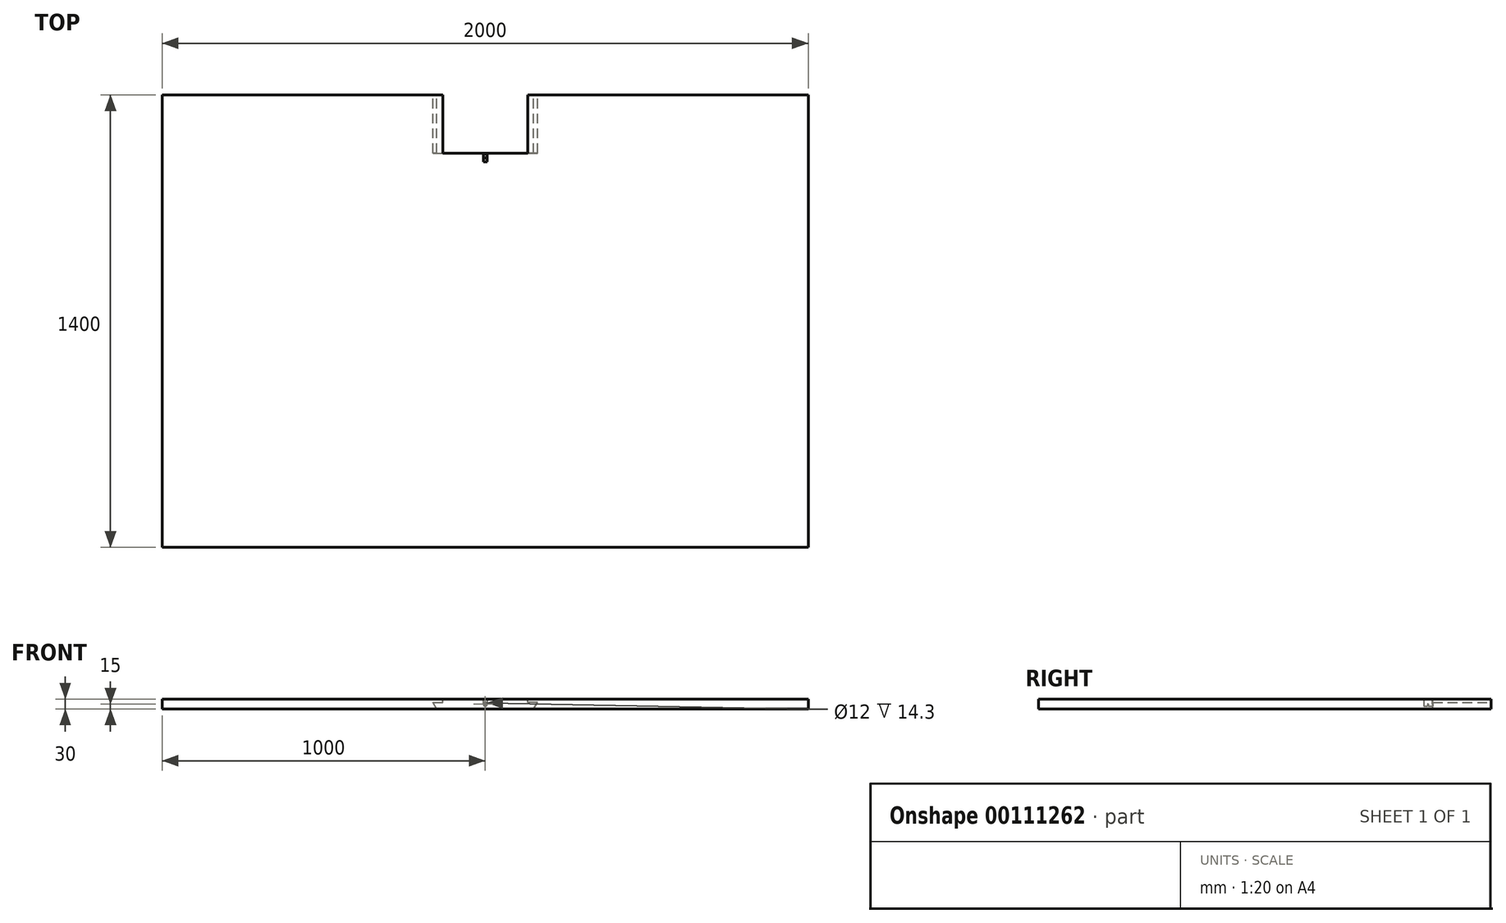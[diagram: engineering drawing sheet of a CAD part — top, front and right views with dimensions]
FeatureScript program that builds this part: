
annotation { "Feature Type Name" : "Feature", "Feature Type Description" : "" }
export const myFeature = defineFeature(function(context is Context, id is Id, definition is map)
    precondition{}
    {
        {
            var Q0;
            Q0=qCreatedBy(makeId("Top.planeOp"),FACE);
            var sketch = newSketch(context, id + "F0", { "sketchPlane" : qUnion([Q0]), "disableImprinting" : false});
            skLineSegment(sketch, "E0.bottom", {"start": v(-1000, 700) * mm, "end": v(1000, 700) * mm});
            skLineSegment(sketch, "E0.top", {"start": v(-1000, -700) * mm, "end": v(1000, -700) * mm});
            skLineSegment(sketch, "E0.left", {"start": v(-1000, 700) * mm, "end": v(-1000, -700) * mm});
            skLineSegment(sketch, "E0.right", {"start": v(1000, 700) * mm, "end": v(1000, -700) * mm});
            skPoint(sketch, "E0.middle", {"position": v(0, 0) * mm});
            skSolve(sketch);
        }
        {
            var Q0;
            Q0=makeQuery(id+"F0.imprint","IMPRINT",FACE,{"disambiguationData":[TD([[makeQuery(id+"F0.imprint","IMPRINT",EDGE,{"derivedFrom":sQuery(id+"F0.wireOp",EDGE,"E0.bottom")}),-1.0]])]});
            extrude(context, id + "F1", {"entities" : qUnion([Q0]), "depth" : 30 * mm});
        }
        {
            var Q0;
            Q0=makeQuery(id+"F1.opExtrude","SWEPT_FACE",FACE,{"disambiguationData":[OSD([sQuery(id+"F0.wireOp",EDGE,"E0.bottom")])]});
            var sketch = newSketch(context, id + "F2", { "sketchPlane" : qUnion([Q0])});
            skLineSegment(sketch, "E1", {"start": v(-150, 0) * mm, "end": v(-161.55, 20) * mm});
            skLineSegment(sketch, "E2", {"start": v(-161.55, 20) * mm, "end": v(-131.55, 20) * mm});
            skLineSegment(sketch, "E3", {"start": v(-131.55, 20) * mm, "end": v(-131.55, 30) * mm});
            skLineSegment(sketch, "E4", {"start": v(0, 0) * mm, "end": v(0, 30) * mm, "construction": true});
            skLineSegment(sketch, "E5.MirrorCS", {"start": v(131.55, 20) * mm, "end": v(131.55, 30) * mm});
            skLineSegment(sketch, "E6.MirrorCS", {"start": v(161.55, 20) * mm, "end": v(131.55, 20) * mm});
            skLineSegment(sketch, "E7.MirrorCS", {"start": v(150, 0) * mm, "end": v(161.55, 20) * mm});
            skLineSegment(sketch, "E8", {"start": v(131.55, 30) * mm, "end": v(-131.55, 30) * mm});
            skLineSegment(sketch, "E9", {"start": v(150, 0) * mm, "end": v(-150, 0) * mm});
            skSolve(sketch);
        }
        {
            var Q0;
            Q0=qSketchRegion(id+"F2",true);
            extrude(context, id + "F3", {"entities" : qUnion([Q0]), "operationType" : NewBodyOperationType.REMOVE, "oppositeDirection" : true, "depth" : 180 * mm});
        }
        {
            var Q0;
            Q0=makeQuery(id+"F3.boolean.opBoolean","COPY",FACE,{"derivedFrom":makeQuery(id+"F3.opExtrude","CAP_FACE",FACE,{"disambiguationData":[OSD([sQuery(id+"F2.wireOp",EDGE,"E1"),sQuery(id+"F2.wireOp",EDGE,"E2"),sQuery(id+"F2.wireOp",EDGE,"E3"),sQuery(id+"F2.wireOp",EDGE,"E5.MirrorCS"),sQuery(id+"F2.wireOp",EDGE,"E6.MirrorCS"),sQuery(id+"F2.wireOp",EDGE,"E7.MirrorCS"),sQuery(id+"F2.wireOp",EDGE,"E8"),sQuery(id+"F2.wireOp",EDGE,"E9")])],"isStart":false})});
            var sketch = newSketch(context, id + "F4", { "sketchPlane" : qUnion([Q0])});
            skLineSegment(sketch, "E10", {"start": v(0, 0) * mm, "end": v(0, 30) * mm, "construction": true});
            skCircle(sketch, "E11", {"center": v(0, 15) * mm, "radius": 6 * mm});
            skSolve(sketch);
        }
        {
            var Q0;
            Q0 = qSketchRegion(id + "F4", true);
            extrude(context, id + "F5", {"entities" : qUnion([Q0]), "operationType" : NewBodyOperationType.REMOVE, "oppositeDirection" : true, "depth" : 20 * mm});
        }
        {
            var Q0;
            Q0=makeQuery(id+"F1.opExtrude","CAP_FACE",FACE,{"disambiguationData":[OSD([sQuery(id+"F0.wireOp",EDGE,"E0.bottom"),sQuery(id+"F0.wireOp",EDGE,"E0.top"),sQuery(id+"F0.wireOp",EDGE,"E0.left"),sQuery(id+"F0.wireOp",EDGE,"E0.right")])],"isStart":true});
            var sketch = newSketch(context, id + "F6", { "sketchPlane" : qUnion([Q0])});
            skLineSegment(sketch, "E12.0", {"start": v(-150, -520) * mm, "end": v(150, -520) * mm, "construction": true});
            skLineSegment(sketch, "E13", {"start": v(0, -520) * mm, "end": v(0, -505) * mm, "construction": true});
            skPoint(sketch, "E13.endSnap0", {"position": v(0, -520) * mm});
            skLineSegment(sketch, "E14.bottom", {"start": v(20, -500) * mm, "end": v(-20, -500) * mm});
            skLineSegment(sketch, "E14.top", {"start": v(20, -510) * mm, "end": v(-20, -510) * mm});
            skLineSegment(sketch, "E14.left", {"start": v(20, -500) * mm, "end": v(20, -510) * mm});
            skLineSegment(sketch, "E14.right", {"start": v(-20, -500) * mm, "end": v(-20, -510) * mm});
            skPoint(sketch, "E14.middle", {"position": v(0, -505) * mm});
            skSolve(sketch);
        }
        {
            var Q0;
            Q0=makeQuery(id+"F6.imprint","IMPRINT",FACE,{"disambiguationData":[TD([[makeQuery(id+"F6.imprint","IMPRINT",EDGE,{"derivedFrom":sQuery(id+"F6.wireOp",EDGE,"E14.bottom")}),1.0]])]});
            extrude(context, id + "F7", {"entities" : qUnion([Q0]), "operationType" : NewBodyOperationType.REMOVE, "oppositeDirection" : true, "depth" : 2 * mm});
        }
        {
            var Q0;
            Q0=makeQuery(id+"F3.boolean.opBoolean","COPY",FACE,{"derivedFrom":makeQuery(id+"F3.opExtrude","CAP_FACE",FACE,{"disambiguationData":[OSD([sQuery(id+"F2.wireOp",EDGE,"E1"),sQuery(id+"F2.wireOp",EDGE,"E2"),sQuery(id+"F2.wireOp",EDGE,"E3"),sQuery(id+"F2.wireOp",EDGE,"E5.MirrorCS"),sQuery(id+"F2.wireOp",EDGE,"E6.MirrorCS"),sQuery(id+"F2.wireOp",EDGE,"E7.MirrorCS"),sQuery(id+"F2.wireOp",EDGE,"E8"),sQuery(id+"F2.wireOp",EDGE,"E9")])],"isStart":false})});
            cPlane(context, id + "F8", {"entities" : qUnion([Q0]), "cplaneType" : CPlaneType.OFFSET, "offset" : 15 * mm, "oppositeDirection" : true, "width" : 150 * mm, "height" : 150 * mm});
        }
        {
            var Q0;
            Q0=makeQuery(id+"F7.boolean.opBoolean","COPY",FACE,{"derivedFrom":makeQuery(id+"F7.opExtrude","CAP_FACE",FACE,{"disambiguationData":[OSD([sQuery(id+"F6.wireOp",EDGE,"E14.bottom"),sQuery(id+"F6.wireOp",EDGE,"E14.top"),sQuery(id+"F6.wireOp",EDGE,"E14.left"),sQuery(id+"F6.wireOp",EDGE,"E14.right")])],"isStart":false})});
            var sketch = newSketch(context, id + "F9", { "sketchPlane" : qUnion([Q0])});
            skLineSegment(sketch, "E15.bottom", {"start": v(20, -500) * mm, "end": v(-20, -500) * mm});
            skLineSegment(sketch, "E15.top", {"start": v(20, -510) * mm, "end": v(-20, -510) * mm});
            skLineSegment(sketch, "E15.left", {"start": v(20, -500) * mm, "end": v(20, -510) * mm});
            skLineSegment(sketch, "E15.right", {"start": v(-20, -500) * mm, "end": v(-20, -510) * mm});
            skLineSegment(sketch, "E16.0", {"start": v(18.5, -501.5) * mm, "end": v(-18.5, -501.5) * mm});
            skLineSegment(sketch, "E16.1", {"start": v(18.5, -501.5) * mm, "end": v(18.5, -508.5) * mm});
            skLineSegment(sketch, "E16.2", {"start": v(18.5, -508.5) * mm, "end": v(-18.5, -508.5) * mm});
            skLineSegment(sketch, "E16.3", {"start": v(-18.5, -501.5) * mm, "end": v(-18.5, -508.5) * mm});
            skSolve(sketch);
        }
        {
            var Q0;
            Q0=makeQuery(id+"F9.imprint","IMPRINT",FACE,{"disambiguationData":[TD([[makeQuery(id+"F9.imprint","IMPRINT",EDGE,{"derivedFrom":sQuery(id+"F9.wireOp",EDGE,"E16.0")}),1.0]])]});
            extrude(context, id + "F10", {"entities" : qUnion([Q0]), "operationType" : NewBodyOperationType.REMOVE, "endBound" : BoundingType.THROUGH_ALL, "oppositeDirection" : true, "depth" : 25 * mm});
        }
        {
            var Q0;
            Q0=qCreatedBy(id+"F8.planeOp",FACE);
            var sketch = newSketch(context, id + "F11", { "sketchPlane" : qUnion([Q0])});
            skCircle(sketch, "E17.0", {"center": v(0, 15) * mm, "radius": 6 * mm});
            skCircle(sketch, "E18", {"center": v(0, 15) * mm, "radius": 4.5 * mm});
            skLineSegment(sketch, "E19", {"start": v(6, 15) * mm, "end": v(-6, 15) * mm});
            skLineSegment(sketch, "E20", {"start": v(6, 15) * mm, "end": v(6, 30) * mm});
            skLineSegment(sketch, "E21", {"start": v(6, 30) * mm, "end": v(-6, 30) * mm});
            skLineSegment(sketch, "E22", {"start": v(-6, 30) * mm, "end": v(-6, 15) * mm});
            skSolve(sketch);
        }
        {
            var Q0;
            Q0 = qSketchRegion(id + "F6", true);
            var Q1;
            Q1=makeQuery(id+"F7.boolean.opBoolean","COPY",FACE,{"derivedFrom":makeQuery(id+"F7.opExtrude","CAP_FACE",FACE,{"disambiguationData":[OSD([sQuery(id+"F6.wireOp",EDGE,"E14.bottom"),sQuery(id+"F6.wireOp",EDGE,"E14.top"),sQuery(id+"F6.wireOp",EDGE,"E14.left"),sQuery(id+"F6.wireOp",EDGE,"E14.right")])],"isStart":false})});
            extrude(context, id + "F12", {"entities" : qUnion([Q0]), "endBound" : BoundingType.UP_TO_SURFACE, "oppositeDirection" : true, "endBoundEntityFace" : qUnion([Q1]), "depth" : 25 * mm});
        }
        {
            var Q0;
            Q0=makeQuery(id+"F12.opExtrude","CAP_FACE",FACE,{"disambiguationData":[OSD([sQuery(id+"F6.wireOp",EDGE,"E14.bottom"),sQuery(id+"F6.wireOp",EDGE,"E14.top"),sQuery(id+"F6.wireOp",EDGE,"E14.left"),sQuery(id+"F6.wireOp",EDGE,"E14.right")])],"isStart":false});
            var sketch = newSketch(context, id + "F13", { "sketchPlane" : qUnion([Q0])});
            skLineSegment(sketch, "E23.0", {"start": v(-18.5, 501.5) * mm, "end": v(-18.5, 508.5) * mm});
            skLineSegment(sketch, "E23.1", {"start": v(18.5, 508.5) * mm, "end": v(-18.5, 508.5) * mm});
            skLineSegment(sketch, "E23.2", {"start": v(18.5, 501.5) * mm, "end": v(18.5, 508.5) * mm});
            skLineSegment(sketch, "E23.3", {"start": v(18.5, 501.5) * mm, "end": v(-18.5, 501.5) * mm});
            skSolve(sketch);
        }
        {
            var Q0;
            Q0 = qSketchRegion(id + "F13", true);
            var Q1;
            Q1=makeQuery(id+"F1.opExtrude","CAP_FACE",FACE,{"disambiguationData":[OSD([sQuery(id+"F0.wireOp",EDGE,"E0.bottom"),sQuery(id+"F0.wireOp",EDGE,"E0.top"),sQuery(id+"F0.wireOp",EDGE,"E0.left"),sQuery(id+"F0.wireOp",EDGE,"E0.right")])],"isStart":false});
            extrude(context, id + "F14", {"entities" : qUnion([Q0]), "operationType" : NewBodyOperationType.ADD, "endBound" : BoundingType.UP_TO_SURFACE, "endBoundEntityFace" : qUnion([Q1]), "depth" : 25 * mm});
        }
        {
            var Q0;
            {var subQ0=sQuery(id+"F11.wireOp",EDGE,"E20");Q0=makeQuery(id+"F11.imprint","IMPRINT",FACE,{"disambiguationData":[TD([[makeQuery(id+"F11.imprint","IMPRINT",EDGE,{"derivedFrom":subQ0}),1.0]])]});}
            var Q1;
            {var subQ0=sQuery(id+"F11.wireOp",EDGE,"E19");var subQ4=sQuery(id+"F11.wireOp",EDGE,"E18");var subQ5=makeQuery(id+"F11.imprint","INTERSECT",VERTEX,{"disambiguationData":[OD(0.0)],"derivedFrom":[subQ4,subQ0]});Q1=makeQuery(id+"F11.imprint","IMPRINT",FACE,{"disambiguationData":[TD([[makeQuery(id+"F11.imprint","IMPRINT",EDGE,{"disambiguationData":[TD([[subQ5,-1.0]])],"derivedFrom":subQ4}),-1.0]])]});}
            var Q2;
            {var subQ0=sQuery(id+"F11.wireOp",EDGE,"E19");var subQ1=sQuery(id+"F11.wireOp",EDGE,"E18");var subQ2=makeQuery(id+"F11.imprint","INTERSECT",VERTEX,{"disambiguationData":[OD(0.0)],"derivedFrom":[subQ1,subQ0]});Q2=makeQuery(id+"F11.imprint","IMPRINT",FACE,{"disambiguationData":[TD([[makeQuery(id+"F11.imprint","IMPRINT",EDGE,{"disambiguationData":[TD([[subQ2,-1.0]])],"derivedFrom":subQ1}),1.0]])]});}
            var Q3;
            {var subQ0=sQuery(id+"F11.wireOp",EDGE,"E19");var subQ1=sQuery(id+"F11.wireOp",EDGE,"E18");var subQ2=makeQuery(id+"F11.imprint","INTERSECT",VERTEX,{"disambiguationData":[OD(0.0)],"derivedFrom":[subQ1,subQ0]});Q3=makeQuery(id+"F11.imprint","IMPRINT",FACE,{"disambiguationData":[TD([[makeQuery(id+"F11.imprint","IMPRINT",EDGE,{"disambiguationData":[TD([[subQ2,1.0]])],"derivedFrom":subQ1}),1.0]])]});}
            var Q4;
            {var subQ0=sQuery(id+"F11.wireOp",EDGE,"E19");var subQ4=sQuery(id+"F11.wireOp",EDGE,"E18");var subQ5=makeQuery(id+"F11.imprint","INTERSECT",VERTEX,{"disambiguationData":[OD(0.0)],"derivedFrom":[subQ4,subQ0]});Q4=makeQuery(id+"F11.imprint","IMPRINT",FACE,{"disambiguationData":[TD([[makeQuery(id+"F11.imprint","IMPRINT",EDGE,{"disambiguationData":[TD([[subQ5,1.0]])],"derivedFrom":subQ4}),-1.0]])]});}
            var Q5;
            Q5=sQuery(id+"F11.wireOp",EDGE,"E17.0");
            extrude(context, id + "F15", {"entities" : qUnion([Q0, Q1, Q2, Q3, Q4]), "operationType" : NewBodyOperationType.REMOVE, "surfaceEntities" : qUnion([Q5]), "oppositeDirection" : true, "depth" : 25 * mm, "symmetric" : true});
        }
        {
            var Q0;
            {var subQ0=sQuery(id+"F11.wireOp",EDGE,"E19");var subQ4=sQuery(id+"F11.wireOp",EDGE,"E18");var subQ5=makeQuery(id+"F11.imprint","INTERSECT",VERTEX,{"disambiguationData":[OD(0.0)],"derivedFrom":[subQ4,subQ0]});Q0=makeQuery(id+"F11.imprint","IMPRINT",FACE,{"disambiguationData":[TD([[makeQuery(id+"F11.imprint","IMPRINT",EDGE,{"disambiguationData":[TD([[subQ5,1.0]])],"derivedFrom":subQ4}),-1.0]])]});}
            extrude(context, id + "F16", {"entities" : qUnion([Q0]), "operationType" : NewBodyOperationType.ADD, "depth" : 2 * mm, "symmetric" : true});
        }
        {
            var Q0;
            {var subQ0=sQuery(id+"F11.wireOp",EDGE,"E19");var subQ1=sQuery(id+"F11.wireOp",EDGE,"E18");Q0=makeQuery(id+"F16.opExtrude","SWEPT_EDGE",EDGE,{"disambiguationData":[OSD([subQ1,subQ0]),TDD([makeQuery(id+"F11.imprint","INTERSECT",VERTEX,{"disambiguationData":[OD(1.0)],"derivedFrom":[subQ1,subQ0]})])]});}
            var Q1;
            {var subQ0=sQuery(id+"F11.wireOp",EDGE,"E19");Q1=makeQuery(id+"F16.opExtrude","CAP_EDGE",EDGE,{"disambiguationData":[OSD([subQ0]),TDD([makeQuery(id+"F11.imprint","IMPRINT",EDGE,{"disambiguationData":[TD([[makeQuery(id+"F11.imprint","INTERSECT",VERTEX,{"disambiguationData":[OD(1.0)],"derivedFrom":[sQuery(id+"F11.wireOp",EDGE,"E18"),subQ0]}),-1.0]])],"derivedFrom":subQ0})])],"isStart":true});}
            var Q2;
            Q2=makeQuery(id+"F16.opExtrude","CAP_EDGE",EDGE,{"disambiguationData":[OSD([sQuery(id+"F11.wireOp",EDGE,"E18")])],"isStart":false});
            var Q3;
            Q3=makeQuery(id+"F16.opExtrude","CAP_EDGE",EDGE,{"disambiguationData":[OSD([sQuery(id+"F11.wireOp",EDGE,"E18")])],"isStart":true});
            var Q4;
            {var subQ0=sQuery(id+"F11.wireOp",EDGE,"E19");Q4=makeQuery(id+"F16.opExtrude","CAP_EDGE",EDGE,{"disambiguationData":[OSD([subQ0]),TDD([makeQuery(id+"F11.imprint","IMPRINT",EDGE,{"disambiguationData":[TD([[makeQuery(id+"F11.imprint","INTERSECT",VERTEX,{"disambiguationData":[OD(1.0)],"derivedFrom":[sQuery(id+"F11.wireOp",EDGE,"E18"),subQ0]}),-1.0]])],"derivedFrom":subQ0})])],"isStart":false});}
            var Q5;
            {var subQ0=sQuery(id+"F11.wireOp",EDGE,"E19");Q5=makeQuery(id+"F16.opExtrude","CAP_EDGE",EDGE,{"disambiguationData":[OSD([subQ0]),TDD([makeQuery(id+"F11.imprint","IMPRINT",EDGE,{"disambiguationData":[TD([[makeQuery(id+"F11.imprint","INTERSECT",VERTEX,{"disambiguationData":[OD(0.0)],"derivedFrom":[sQuery(id+"F11.wireOp",EDGE,"E18"),subQ0]}),1.0]])],"derivedFrom":subQ0})])],"isStart":false});}
            var Q6;
            {var subQ0=sQuery(id+"F11.wireOp",EDGE,"E19");var subQ1=sQuery(id+"F11.wireOp",EDGE,"E18");Q6=makeQuery(id+"F16.opExtrude","SWEPT_EDGE",EDGE,{"disambiguationData":[OSD([subQ1,subQ0]),TDD([makeQuery(id+"F11.imprint","INTERSECT",VERTEX,{"disambiguationData":[OD(0.0)],"derivedFrom":[subQ1,subQ0]})])]});}
            var Q7;
            {var subQ0=sQuery(id+"F11.wireOp",EDGE,"E19");Q7=makeQuery(id+"F16.opExtrude","CAP_EDGE",EDGE,{"disambiguationData":[OSD([subQ0]),TDD([makeQuery(id+"F11.imprint","IMPRINT",EDGE,{"disambiguationData":[TD([[makeQuery(id+"F11.imprint","INTERSECT",VERTEX,{"disambiguationData":[OD(0.0)],"derivedFrom":[sQuery(id+"F11.wireOp",EDGE,"E18"),subQ0]}),1.0]])],"derivedFrom":subQ0})])],"isStart":true});}
            fillet(context, id + "F17", {"entities" : qUnion([Q0, Q1, Q2, Q3, Q4, Q5, Q6, Q7]), "radius" : 0.3 * mm, "tangentPropagation" : true, "allowEdgeOverflow" : false});
        }
    });
